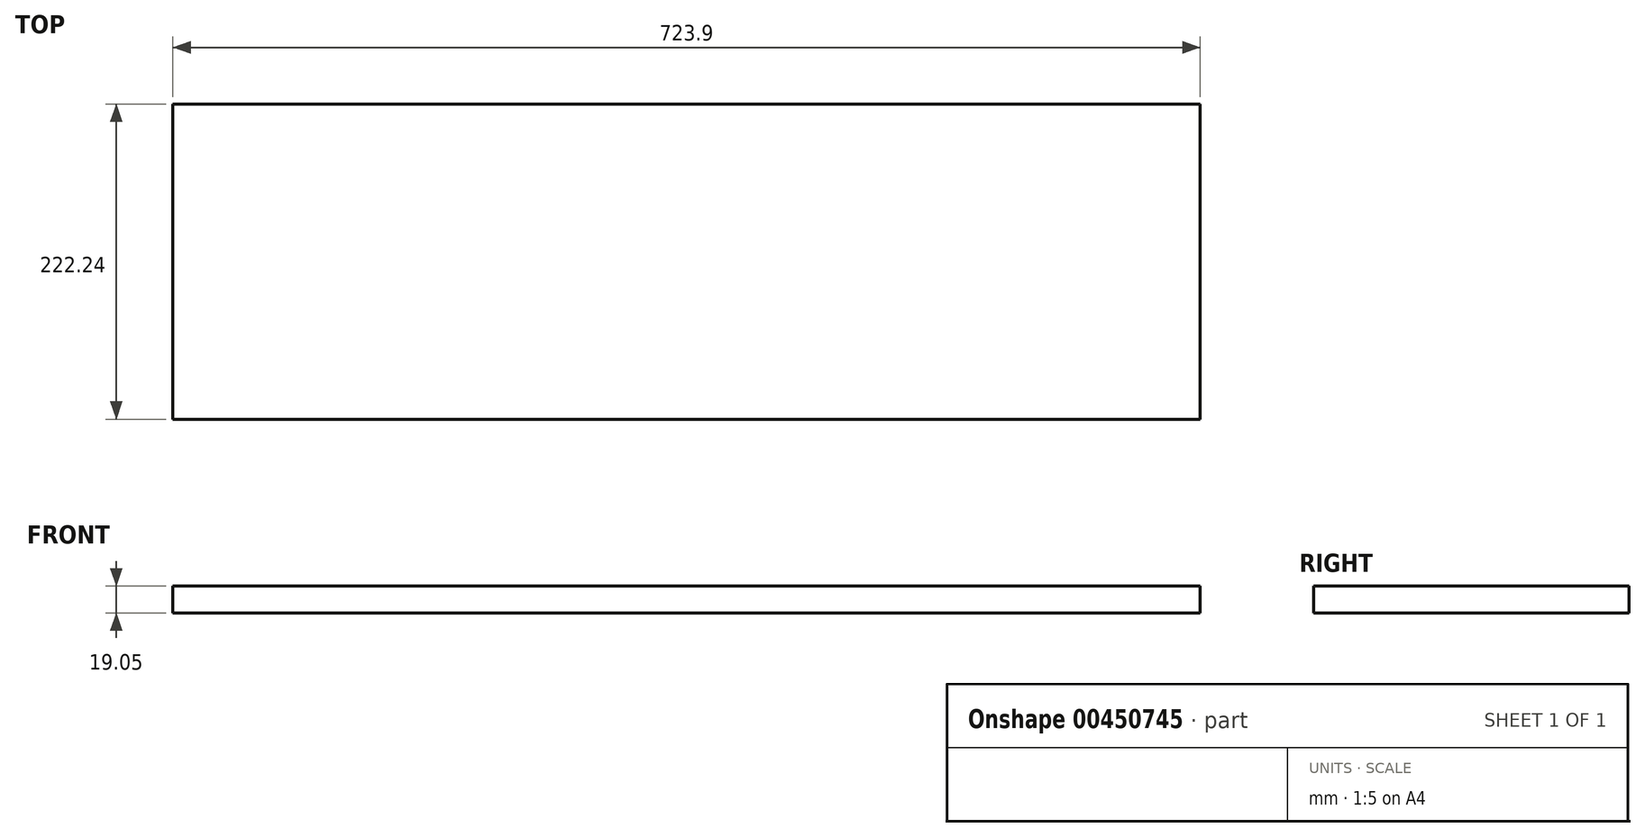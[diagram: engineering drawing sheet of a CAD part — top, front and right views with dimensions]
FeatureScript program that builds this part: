
annotation { "Feature Type Name" : "Feature", "Feature Type Description" : "" }
export const myFeature = defineFeature(function(context is Context, id is Id, definition is map)
    precondition{}
    {
        {
            var Q0;
            Q0=qCreatedBy(makeId("Top.planeOp"),FACE);
            var sketch = newSketch(context, id + "F0", { "sketchPlane" : qUnion([Q0])});
            skLineSegment(sketch, "E0.bottom", {"start": v(-361.95, 111.12) * mm, "end": v(361.95, 111.12) * mm});
            skLineSegment(sketch, "E0.top", {"start": v(-361.95, -111.12) * mm, "end": v(361.95, -111.12) * mm});
            skLineSegment(sketch, "E0.left", {"start": v(-361.95, 111.12) * mm, "end": v(-361.95, -111.12) * mm});
            skLineSegment(sketch, "E0.right", {"start": v(361.95, 111.12) * mm, "end": v(361.95, -111.12) * mm});
            skPoint(sketch, "E0.middle", {"position": v(0, 0) * mm});
            skSolve(sketch);
        }
        {
            var Q0;
            Q0=makeQuery(id+"F0.imprint","IMPRINT",FACE,{"disambiguationData":[TD([[makeQuery(id+"F0.imprint","IMPRINT",EDGE,{"derivedFrom":sQuery(id+"F0.wireOp",EDGE,"E0.bottom")}),-1.0]])]});
            extrude(context, id + "F1", {"entities" : qUnion([Q0]), "depth" : 19.05 * mm});
        }
    });
